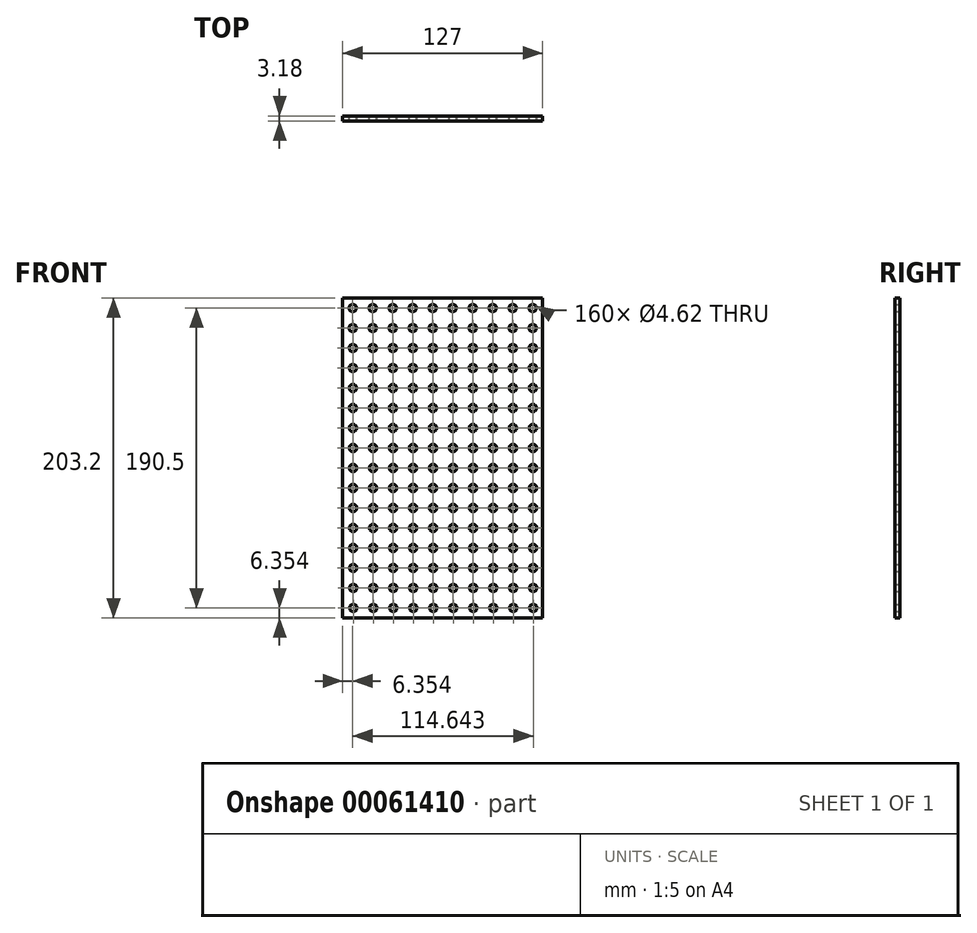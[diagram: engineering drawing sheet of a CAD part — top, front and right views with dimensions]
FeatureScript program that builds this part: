
annotation { "Feature Type Name" : "Feature", "Feature Type Description" : "" }
export const myFeature = defineFeature(function(context is Context, id is Id, definition is map)
    precondition{}
    {
        {
            var Q0;
            Q0=qCreatedBy(makeId("Front.planeOp"),FACE);
            var sketch = newSketch(context, id + "F0", { "sketchPlane" : qUnion([Q0])});
            skLineSegment(sketch, "E0.bottom", {"start": v(-54.39, 98.82) * mm, "end": v(72.61, 98.82) * mm});
            skLineSegment(sketch, "E0.top", {"start": v(-54.39, -104.38) * mm, "end": v(72.61, -104.38) * mm});
            skLineSegment(sketch, "E0.left", {"start": v(-54.39, 98.82) * mm, "end": v(-54.39, -104.38) * mm});
            skLineSegment(sketch, "E0.right", {"start": v(72.61, 98.82) * mm, "end": v(72.61, -104.38) * mm});
            skCircle(sketch, "E1", {"center": v(-48.04, 92.47) * mm, "radius": 2.31 * mm});
            skLineSegment(sketch, "E2", {"start": v(-54.39, 92.47) * mm, "end": v(-54.39, 98.82) * mm, "construction": true});
            skLineSegment(sketch, "E3", {"start": v(-54.39, 98.82) * mm, "end": v(-48.04, 98.82) * mm, "construction": true});
            skCircle(sketch, "E4.1.0.0", {"center": v(-35.34, 92.47) * mm, "radius": 2.31 * mm});
            skCircle(sketch, "E4.2.0.0", {"center": v(-22.64, 92.47) * mm, "radius": 2.31 * mm});
            skCircle(sketch, "E4.3.0.0", {"center": v(-9.94, 92.47) * mm, "radius": 2.31 * mm});
            skCircle(sketch, "E4.4.0.0", {"center": v(2.76, 92.47) * mm, "radius": 2.31 * mm});
            skCircle(sketch, "E4.5.0.0", {"center": v(15.46, 92.47) * mm, "radius": 2.31 * mm});
            skCircle(sketch, "E4.6.0.0", {"center": v(28.16, 92.47) * mm, "radius": 2.31 * mm});
            skCircle(sketch, "E4.7.0.0", {"center": v(40.86, 92.47) * mm, "radius": 2.31 * mm});
            skCircle(sketch, "E4.8.0.0", {"center": v(53.56, 92.47) * mm, "radius": 2.31 * mm});
            skCircle(sketch, "E4.9.0.0", {"center": v(66.26, 92.47) * mm, "radius": 2.31 * mm});
            skLineSegment(sketch, "E4.direction1", {"start": v(-48.04, 92.47) * mm, "end": v(-35.34, 92.47) * mm, "construction": true});
            skCircle(sketch, "E5.1.0.0", {"center": v(-48.01, 79.77) * mm, "radius": 2.31 * mm});
            skCircle(sketch, "E5.2.0.0", {"center": v(-48, 67.07) * mm, "radius": 2.31 * mm});
            skCircle(sketch, "E5.3.0.0", {"center": v(-47.97, 54.37) * mm, "radius": 2.31 * mm});
            skCircle(sketch, "E5.4.0.0", {"center": v(-47.94, 41.67) * mm, "radius": 2.31 * mm});
            skCircle(sketch, "E5.5.0.0", {"center": v(-47.92, 28.97) * mm, "radius": 2.31 * mm});
            skCircle(sketch, "E5.6.0.0", {"center": v(-47.9, 16.27) * mm, "radius": 2.31 * mm});
            skCircle(sketch, "E5.7.0.0", {"center": v(-47.88, 3.57) * mm, "radius": 2.31 * mm});
            skCircle(sketch, "E5.8.0.0", {"center": v(-47.85, -9.13) * mm, "radius": 2.31 * mm});
            skCircle(sketch, "E5.9.0.0", {"center": v(-47.83, -21.83) * mm, "radius": 2.31 * mm});
            skCircle(sketch, "E5.10.0.0", {"center": v(-47.8, -34.53) * mm, "radius": 2.31 * mm});
            skCircle(sketch, "E5.11.0.0", {"center": v(-47.78, -47.23) * mm, "radius": 2.31 * mm});
            skCircle(sketch, "E5.12.0.0", {"center": v(-47.76, -59.93) * mm, "radius": 2.31 * mm});
            skCircle(sketch, "E5.13.0.0", {"center": v(-47.74, -72.63) * mm, "radius": 2.31 * mm});
            skCircle(sketch, "E5.14.0.0", {"center": v(-47.72, -85.33) * mm, "radius": 2.31 * mm});
            skLineSegment(sketch, "E5.direction1", {"start": v(-48.04, 92.47) * mm, "end": v(-48.01, 79.77) * mm, "construction": true});
            skCircle(sketch, "E6.0.15.0", {"center": v(-47.7, -98.03) * mm, "radius": 2.31 * mm});
            skCircle(sketch, "E7.1.0.0", {"center": v(-35.31, 79.77) * mm, "radius": 2.31 * mm});
            skCircle(sketch, "E7.2.0.0", {"center": v(-22.61, 79.77) * mm, "radius": 2.31 * mm});
            skCircle(sketch, "E7.3.0.0", {"center": v(-9.91, 79.77) * mm, "radius": 2.31 * mm});
            skCircle(sketch, "E7.4.0.0", {"center": v(2.79, 79.77) * mm, "radius": 2.31 * mm});
            skCircle(sketch, "E7.5.0.0", {"center": v(15.49, 79.77) * mm, "radius": 2.31 * mm});
            skCircle(sketch, "E7.6.0.0", {"center": v(28.19, 79.77) * mm, "radius": 2.31 * mm});
            skCircle(sketch, "E7.7.0.0", {"center": v(40.89, 79.77) * mm, "radius": 2.31 * mm});
            skCircle(sketch, "E7.8.0.0", {"center": v(53.59, 79.77) * mm, "radius": 2.31 * mm});
            skCircle(sketch, "E7.9.0.0", {"center": v(66.29, 79.77) * mm, "radius": 2.31 * mm});
            skLineSegment(sketch, "E7.direction1", {"start": v(-48.01, 79.77) * mm, "end": v(-35.31, 79.77) * mm, "construction": true});
            skCircle(sketch, "E8.1.0.0", {"center": v(-35.3, 67.07) * mm, "radius": 2.31 * mm});
            skCircle(sketch, "E8.2.0.0", {"center": v(-22.6, 67.07) * mm, "radius": 2.31 * mm});
            skCircle(sketch, "E8.3.0.0", {"center": v(-9.9, 67.07) * mm, "radius": 2.31 * mm});
            skCircle(sketch, "E8.4.0.0", {"center": v(2.8, 67.07) * mm, "radius": 2.31 * mm});
            skCircle(sketch, "E8.5.0.0", {"center": v(15.5, 67.07) * mm, "radius": 2.31 * mm});
            skCircle(sketch, "E8.6.0.0", {"center": v(28.2, 67.07) * mm, "radius": 2.31 * mm});
            skCircle(sketch, "E8.7.0.0", {"center": v(40.9, 67.07) * mm, "radius": 2.31 * mm});
            skCircle(sketch, "E8.8.0.0", {"center": v(53.6, 67.07) * mm, "radius": 2.31 * mm});
            skCircle(sketch, "E8.9.0.0", {"center": v(66.3, 67.07) * mm, "radius": 2.31 * mm});
            skLineSegment(sketch, "E8.direction1", {"start": v(-48, 67.07) * mm, "end": v(-35.3, 67.07) * mm, "construction": true});
            skCircle(sketch, "E9.1.0.0", {"center": v(-35.27, 54.37) * mm, "radius": 2.31 * mm});
            skCircle(sketch, "E9.2.0.0", {"center": v(-22.57, 54.37) * mm, "radius": 2.31 * mm});
            skCircle(sketch, "E9.3.0.0", {"center": v(-9.87, 54.37) * mm, "radius": 2.31 * mm});
            skCircle(sketch, "E9.4.0.0", {"center": v(2.83, 54.37) * mm, "radius": 2.31 * mm});
            skCircle(sketch, "E9.5.0.0", {"center": v(15.53, 54.37) * mm, "radius": 2.31 * mm});
            skCircle(sketch, "E9.6.0.0", {"center": v(28.23, 54.37) * mm, "radius": 2.31 * mm});
            skCircle(sketch, "E9.7.0.0", {"center": v(40.93, 54.37) * mm, "radius": 2.31 * mm});
            skCircle(sketch, "E9.8.0.0", {"center": v(53.63, 54.37) * mm, "radius": 2.31 * mm});
            skCircle(sketch, "E9.9.0.0", {"center": v(66.33, 54.37) * mm, "radius": 2.31 * mm});
            skLineSegment(sketch, "E9.direction1", {"start": v(-47.97, 54.37) * mm, "end": v(-35.27, 54.37) * mm, "construction": true});
            skCircle(sketch, "E10.1.0.0", {"center": v(-35.24, 41.67) * mm, "radius": 2.31 * mm});
            skCircle(sketch, "E10.2.0.0", {"center": v(-22.54, 41.67) * mm, "radius": 2.31 * mm});
            skCircle(sketch, "E10.3.0.0", {"center": v(-9.84, 41.67) * mm, "radius": 2.31 * mm});
            skCircle(sketch, "E10.4.0.0", {"center": v(2.86, 41.67) * mm, "radius": 2.31 * mm});
            skCircle(sketch, "E10.5.0.0", {"center": v(15.56, 41.67) * mm, "radius": 2.31 * mm});
            skCircle(sketch, "E10.6.0.0", {"center": v(28.26, 41.67) * mm, "radius": 2.31 * mm});
            skCircle(sketch, "E10.7.0.0", {"center": v(40.96, 41.67) * mm, "radius": 2.31 * mm});
            skCircle(sketch, "E10.8.0.0", {"center": v(53.66, 41.67) * mm, "radius": 2.31 * mm});
            skCircle(sketch, "E10.9.0.0", {"center": v(66.36, 41.67) * mm, "radius": 2.31 * mm});
            skLineSegment(sketch, "E10.direction1", {"start": v(-47.94, 41.67) * mm, "end": v(-35.24, 41.67) * mm, "construction": true});
            skCircle(sketch, "E11.1.0.0", {"center": v(-35.22, 28.97) * mm, "radius": 2.31 * mm});
            skCircle(sketch, "E11.2.0.0", {"center": v(-22.52, 28.97) * mm, "radius": 2.31 * mm});
            skCircle(sketch, "E11.3.0.0", {"center": v(-9.82, 28.97) * mm, "radius": 2.31 * mm});
            skCircle(sketch, "E11.4.0.0", {"center": v(2.88, 28.97) * mm, "radius": 2.31 * mm});
            skCircle(sketch, "E11.5.0.0", {"center": v(15.58, 28.97) * mm, "radius": 2.31 * mm});
            skCircle(sketch, "E11.6.0.0", {"center": v(28.28, 28.97) * mm, "radius": 2.31 * mm});
            skCircle(sketch, "E11.7.0.0", {"center": v(40.98, 28.97) * mm, "radius": 2.31 * mm});
            skCircle(sketch, "E11.8.0.0", {"center": v(53.68, 28.97) * mm, "radius": 2.31 * mm});
            skCircle(sketch, "E11.9.0.0", {"center": v(66.38, 28.97) * mm, "radius": 2.31 * mm});
            skLineSegment(sketch, "E11.direction1", {"start": v(-47.92, 28.97) * mm, "end": v(-35.22, 28.97) * mm, "construction": true});
            skCircle(sketch, "E12.1.0.0", {"center": v(-35.2, 16.27) * mm, "radius": 2.31 * mm});
            skCircle(sketch, "E12.2.0.0", {"center": v(-22.5, 16.27) * mm, "radius": 2.31 * mm});
            skCircle(sketch, "E12.3.0.0", {"center": v(-9.8, 16.27) * mm, "radius": 2.31 * mm});
            skCircle(sketch, "E12.4.0.0", {"center": v(2.9, 16.27) * mm, "radius": 2.31 * mm});
            skCircle(sketch, "E12.5.0.0", {"center": v(15.6, 16.27) * mm, "radius": 2.31 * mm});
            skCircle(sketch, "E12.6.0.0", {"center": v(28.3, 16.27) * mm, "radius": 2.31 * mm});
            skCircle(sketch, "E12.7.0.0", {"center": v(41, 16.27) * mm, "radius": 2.31 * mm});
            skCircle(sketch, "E12.8.0.0", {"center": v(53.7, 16.27) * mm, "radius": 2.31 * mm});
            skCircle(sketch, "E12.9.0.0", {"center": v(66.4, 16.27) * mm, "radius": 2.31 * mm});
            skLineSegment(sketch, "E12.direction1", {"start": v(-47.9, 16.27) * mm, "end": v(-35.2, 16.27) * mm, "construction": true});
            skCircle(sketch, "E13.1.0.0", {"center": v(-35.18, 3.57) * mm, "radius": 2.31 * mm});
            skCircle(sketch, "E13.1.0.1", {"center": v(-35.15, -9.13) * mm, "radius": 2.31 * mm});
            skCircle(sketch, "E13.1.0.2", {"center": v(-35.13, -21.83) * mm, "radius": 2.31 * mm});
            skCircle(sketch, "E13.1.0.3", {"center": v(-35.1, -34.53) * mm, "radius": 2.31 * mm});
            skCircle(sketch, "E13.1.0.4", {"center": v(-35.08, -47.23) * mm, "radius": 2.31 * mm});
            skCircle(sketch, "E13.1.0.5", {"center": v(-35.06, -59.93) * mm, "radius": 2.31 * mm});
            skCircle(sketch, "E13.1.0.6", {"center": v(-35.04, -72.63) * mm, "radius": 2.31 * mm});
            skCircle(sketch, "E13.1.0.7", {"center": v(-35.02, -85.33) * mm, "radius": 2.31 * mm});
            skCircle(sketch, "E13.1.0.8", {"center": v(-35, -98.03) * mm, "radius": 2.31 * mm});
            skCircle(sketch, "E13.2.0.0", {"center": v(-22.48, 3.57) * mm, "radius": 2.31 * mm});
            skCircle(sketch, "E13.2.0.1", {"center": v(-22.45, -9.13) * mm, "radius": 2.31 * mm});
            skCircle(sketch, "E13.2.0.2", {"center": v(-22.43, -21.83) * mm, "radius": 2.31 * mm});
            skCircle(sketch, "E13.2.0.3", {"center": v(-22.4, -34.53) * mm, "radius": 2.31 * mm});
            skCircle(sketch, "E13.2.0.4", {"center": v(-22.38, -47.23) * mm, "radius": 2.31 * mm});
            skCircle(sketch, "E13.2.0.5", {"center": v(-22.36, -59.93) * mm, "radius": 2.31 * mm});
            skCircle(sketch, "E13.2.0.6", {"center": v(-22.34, -72.63) * mm, "radius": 2.31 * mm});
            skCircle(sketch, "E13.2.0.7", {"center": v(-22.32, -85.33) * mm, "radius": 2.31 * mm});
            skCircle(sketch, "E13.2.0.8", {"center": v(-22.3, -98.03) * mm, "radius": 2.31 * mm});
            skCircle(sketch, "E13.3.0.0", {"center": v(-9.78, 3.57) * mm, "radius": 2.31 * mm});
            skCircle(sketch, "E13.3.0.1", {"center": v(-9.75, -9.13) * mm, "radius": 2.31 * mm});
            skCircle(sketch, "E13.3.0.2", {"center": v(-9.73, -21.83) * mm, "radius": 2.31 * mm});
            skCircle(sketch, "E13.3.0.3", {"center": v(-9.7, -34.53) * mm, "radius": 2.31 * mm});
            skCircle(sketch, "E13.3.0.4", {"center": v(-9.68, -47.23) * mm, "radius": 2.31 * mm});
            skCircle(sketch, "E13.3.0.5", {"center": v(-9.66, -59.93) * mm, "radius": 2.31 * mm});
            skCircle(sketch, "E13.3.0.6", {"center": v(-9.64, -72.63) * mm, "radius": 2.31 * mm});
            skCircle(sketch, "E13.3.0.7", {"center": v(-9.62, -85.33) * mm, "radius": 2.31 * mm});
            skCircle(sketch, "E13.3.0.8", {"center": v(-9.6, -98.03) * mm, "radius": 2.31 * mm});
            skCircle(sketch, "E13.4.0.0", {"center": v(2.92, 3.57) * mm, "radius": 2.31 * mm});
            skCircle(sketch, "E13.4.0.1", {"center": v(2.95, -9.13) * mm, "radius": 2.31 * mm});
            skCircle(sketch, "E13.4.0.2", {"center": v(2.97, -21.83) * mm, "radius": 2.31 * mm});
            skCircle(sketch, "E13.4.0.3", {"center": v(3, -34.53) * mm, "radius": 2.31 * mm});
            skCircle(sketch, "E13.4.0.4", {"center": v(3.02, -47.23) * mm, "radius": 2.31 * mm});
            skCircle(sketch, "E13.4.0.5", {"center": v(3.04, -59.93) * mm, "radius": 2.31 * mm});
            skCircle(sketch, "E13.4.0.6", {"center": v(3.06, -72.63) * mm, "radius": 2.31 * mm});
            skCircle(sketch, "E13.4.0.7", {"center": v(3.08, -85.33) * mm, "radius": 2.31 * mm});
            skCircle(sketch, "E13.4.0.8", {"center": v(3.1, -98.03) * mm, "radius": 2.31 * mm});
            skCircle(sketch, "E13.5.0.0", {"center": v(15.62, 3.57) * mm, "radius": 2.31 * mm});
            skCircle(sketch, "E13.5.0.1", {"center": v(15.65, -9.13) * mm, "radius": 2.31 * mm});
            skCircle(sketch, "E13.5.0.2", {"center": v(15.67, -21.83) * mm, "radius": 2.31 * mm});
            skCircle(sketch, "E13.5.0.3", {"center": v(15.7, -34.53) * mm, "radius": 2.31 * mm});
            skCircle(sketch, "E13.5.0.4", {"center": v(15.72, -47.23) * mm, "radius": 2.31 * mm});
            skCircle(sketch, "E13.5.0.5", {"center": v(15.74, -59.93) * mm, "radius": 2.31 * mm});
            skCircle(sketch, "E13.5.0.6", {"center": v(15.76, -72.63) * mm, "radius": 2.31 * mm});
            skCircle(sketch, "E13.5.0.7", {"center": v(15.78, -85.33) * mm, "radius": 2.31 * mm});
            skCircle(sketch, "E13.5.0.8", {"center": v(15.8, -98.03) * mm, "radius": 2.31 * mm});
            skCircle(sketch, "E13.6.0.0", {"center": v(28.32, 3.57) * mm, "radius": 2.31 * mm});
            skCircle(sketch, "E13.6.0.1", {"center": v(28.35, -9.13) * mm, "radius": 2.31 * mm});
            skCircle(sketch, "E13.6.0.2", {"center": v(28.37, -21.83) * mm, "radius": 2.31 * mm});
            skCircle(sketch, "E13.6.0.3", {"center": v(28.4, -34.53) * mm, "radius": 2.31 * mm});
            skCircle(sketch, "E13.6.0.4", {"center": v(28.42, -47.23) * mm, "radius": 2.31 * mm});
            skCircle(sketch, "E13.6.0.5", {"center": v(28.44, -59.93) * mm, "radius": 2.31 * mm});
            skCircle(sketch, "E13.6.0.6", {"center": v(28.46, -72.63) * mm, "radius": 2.31 * mm});
            skCircle(sketch, "E13.6.0.7", {"center": v(28.48, -85.33) * mm, "radius": 2.31 * mm});
            skCircle(sketch, "E13.6.0.8", {"center": v(28.5, -98.03) * mm, "radius": 2.31 * mm});
            skCircle(sketch, "E13.7.0.0", {"center": v(41.02, 3.57) * mm, "radius": 2.31 * mm});
            skCircle(sketch, "E13.7.0.1", {"center": v(41.05, -9.13) * mm, "radius": 2.31 * mm});
            skCircle(sketch, "E13.7.0.2", {"center": v(41.07, -21.83) * mm, "radius": 2.31 * mm});
            skCircle(sketch, "E13.7.0.3", {"center": v(41.1, -34.53) * mm, "radius": 2.31 * mm});
            skCircle(sketch, "E13.7.0.4", {"center": v(41.12, -47.23) * mm, "radius": 2.31 * mm});
            skCircle(sketch, "E13.7.0.5", {"center": v(41.14, -59.93) * mm, "radius": 2.31 * mm});
            skCircle(sketch, "E13.7.0.6", {"center": v(41.16, -72.63) * mm, "radius": 2.31 * mm});
            skCircle(sketch, "E13.7.0.7", {"center": v(41.18, -85.33) * mm, "radius": 2.31 * mm});
            skCircle(sketch, "E13.7.0.8", {"center": v(41.2, -98.03) * mm, "radius": 2.31 * mm});
            skCircle(sketch, "E13.8.0.0", {"center": v(53.72, 3.57) * mm, "radius": 2.31 * mm});
            skCircle(sketch, "E13.8.0.1", {"center": v(53.75, -9.13) * mm, "radius": 2.31 * mm});
            skCircle(sketch, "E13.8.0.2", {"center": v(53.77, -21.83) * mm, "radius": 2.31 * mm});
            skCircle(sketch, "E13.8.0.3", {"center": v(53.8, -34.53) * mm, "radius": 2.31 * mm});
            skCircle(sketch, "E13.8.0.4", {"center": v(53.82, -47.23) * mm, "radius": 2.31 * mm});
            skCircle(sketch, "E13.8.0.5", {"center": v(53.84, -59.93) * mm, "radius": 2.31 * mm});
            skCircle(sketch, "E13.8.0.6", {"center": v(53.86, -72.63) * mm, "radius": 2.31 * mm});
            skCircle(sketch, "E13.8.0.7", {"center": v(53.88, -85.33) * mm, "radius": 2.31 * mm});
            skCircle(sketch, "E13.8.0.8", {"center": v(53.9, -98.03) * mm, "radius": 2.31 * mm});
            skCircle(sketch, "E13.9.0.0", {"center": v(66.42, 3.57) * mm, "radius": 2.31 * mm});
            skCircle(sketch, "E13.9.0.1", {"center": v(66.45, -9.13) * mm, "radius": 2.31 * mm});
            skCircle(sketch, "E13.9.0.2", {"center": v(66.47, -21.83) * mm, "radius": 2.31 * mm});
            skCircle(sketch, "E13.9.0.3", {"center": v(66.5, -34.53) * mm, "radius": 2.31 * mm});
            skCircle(sketch, "E13.9.0.4", {"center": v(66.52, -47.23) * mm, "radius": 2.31 * mm});
            skCircle(sketch, "E13.9.0.5", {"center": v(66.54, -59.93) * mm, "radius": 2.31 * mm});
            skCircle(sketch, "E13.9.0.6", {"center": v(66.56, -72.63) * mm, "radius": 2.31 * mm});
            skCircle(sketch, "E13.9.0.7", {"center": v(66.58, -85.33) * mm, "radius": 2.31 * mm});
            skCircle(sketch, "E13.9.0.8", {"center": v(66.6, -98.03) * mm, "radius": 2.31 * mm});
            skLineSegment(sketch, "E13.direction1", {"start": v(-47.88, 3.57) * mm, "end": v(-35.18, 3.57) * mm, "construction": true});
            skSolve(sketch);
        }
        {
            var Q0;
            Q0=makeQuery(id+"F0.imprint","IMPRINT",FACE,{"disambiguationData":[TD([[makeQuery(id+"F0.imprint","IMPRINT",EDGE,{"derivedFrom":sQuery(id+"F0.wireOp",EDGE,"E0.bottom")}),-1.0]])]});
            extrude(context, id + "F1", {"entities" : qUnion([Q0]), "depth" : 3.17 * mm});
        }
    });
